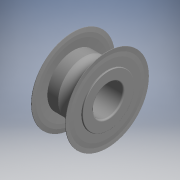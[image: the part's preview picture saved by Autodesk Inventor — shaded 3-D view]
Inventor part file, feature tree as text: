
AUTODESK INVENTOR PART (.ipt)
format: ipt  version: 2017.3 (Build 213256000, 256)  size: 186,368 bytes
history: native  units: mm (DEFAULTED — no unit token found)
features: revolve x3, sketch x3
ambient origin geometry x8: Origin, YZ Plane, XZ Plane, XY Plane, X Axis, Y Axis, Z Axis, Center Point
bodies: Solid1 (feature_tree)
feature tree (6):
  revolve  "Revolution1"  Angle=360.0deg
  revolve  "Revolution2"  [1 undecoded]
  revolve  "Revolution3"  [1 undecoded]
  sketch  "Sketch_62"  dims[d0=360.0deg d1=360.0deg]
  sketch  "Sketch_63"  dims[d2=360.0deg]
  sketch  "Sketch_65"
note: 2 required parameter values undecoded (feature->parameter linkage not recoverable at this tier; creation-order binding heuristic only, values carry confidence <= 0.55)
